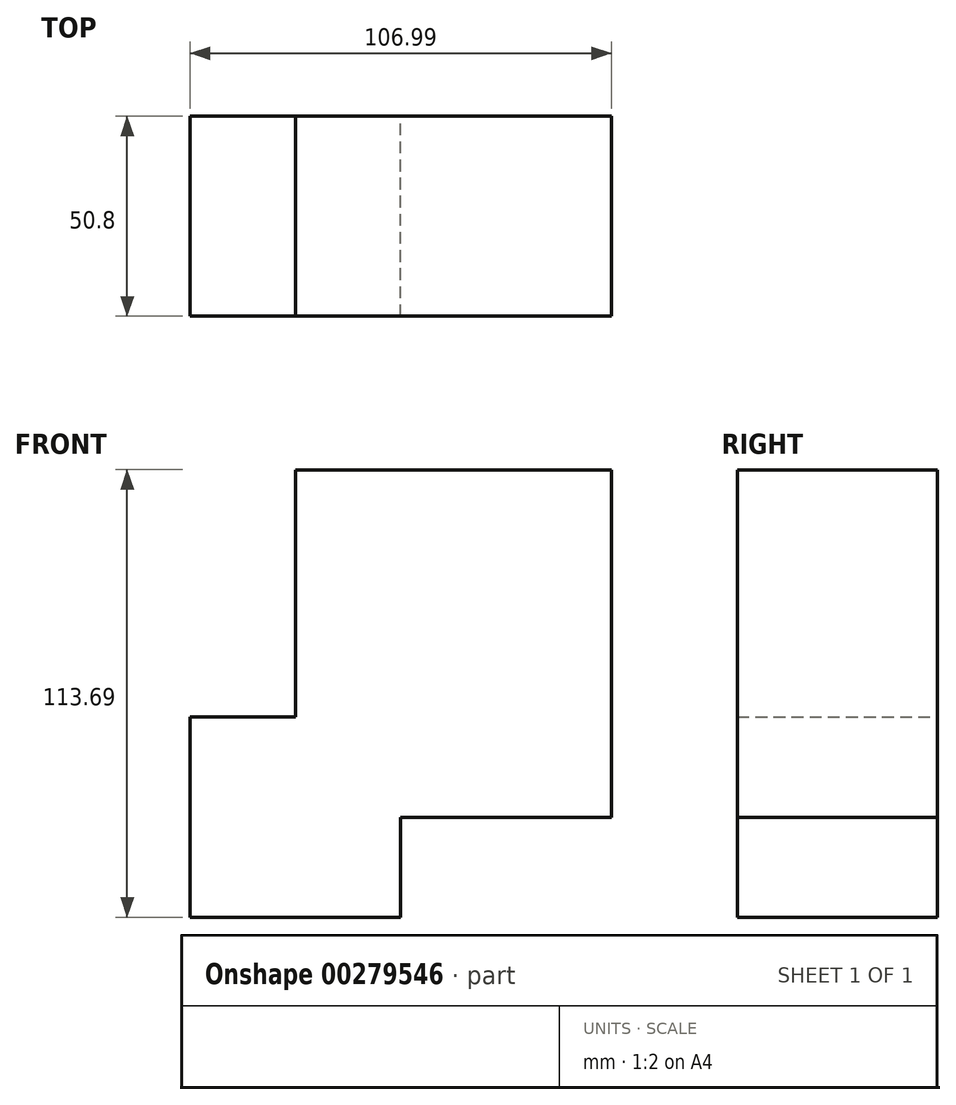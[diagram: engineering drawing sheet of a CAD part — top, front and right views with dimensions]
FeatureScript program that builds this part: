
annotation { "Feature Type Name" : "Feature", "Feature Type Description" : "" }
export const myFeature = defineFeature(function(context is Context, id is Id, definition is map)
    precondition{}
    {
        {
            var Q0;
            Q0=qCreatedBy(makeId("Front.planeOp"),FACE);
            var sketch = newSketch(context, id + "F0", { "sketchPlane" : qUnion([Q0])});
            skLineSegment(sketch, "E0.bottom", {"start": v(-40.12, -44.14) * mm, "end": v(40.12, -44.14) * mm});
            skLineSegment(sketch, "E0.top", {"start": v(-40.12, 44.14) * mm, "end": v(40.12, 44.14) * mm});
            skLineSegment(sketch, "E0.left", {"start": v(-40.12, -44.14) * mm, "end": v(-40.12, 44.14) * mm});
            skLineSegment(sketch, "E0.right", {"start": v(40.12, -44.14) * mm, "end": v(40.12, 44.14) * mm});
            skPoint(sketch, "E0.middle", {"position": v(0, 0) * mm});
            skLineSegment(sketch, "E1.bottom", {"start": v(-66.87, -18.72) * mm, "end": v(-13.37, -18.72) * mm});
            skLineSegment(sketch, "E1.top", {"start": v(-66.87, -69.55) * mm, "end": v(-13.37, -69.55) * mm});
            skLineSegment(sketch, "E1.left", {"start": v(-66.87, -18.72) * mm, "end": v(-66.87, -69.55) * mm});
            skLineSegment(sketch, "E1.right", {"start": v(-13.37, -18.72) * mm, "end": v(-13.37, -69.55) * mm});
            skPoint(sketch, "E1.middle", {"position": v(-40.12, -44.14) * mm});
            skSolve(sketch);
        }
        {
            var Q0;
            Q0 = qSketchRegion(id + "F0", true);
            extrude(context, id + "F1", {"entities" : qUnion([Q0]), "depth" : 50.8 * mm});
        }
    });
